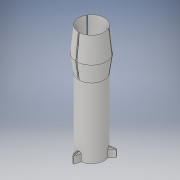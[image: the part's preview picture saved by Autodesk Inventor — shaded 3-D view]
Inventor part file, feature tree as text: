
AUTODESK INVENTOR PART (.ipt)
format: ipt  version: 2017 (Build 210142000, 142)  size: 195,072 bytes
history: native  units: in
note: dims shown in document units (in); Inventor stores cm internally (conversion verified against a paired STEP export)
features: sketch x2, extrude x2, revolve x1, chamfer x1
ambient origin geometry x8: Origin, YZ Plane, XZ Plane, XY Plane, X Axis, Y Axis, Z Axis, Center Point
bodies: Solid1 (feature_tree)
feature tree (6):
  revolve  "Revolution1"  [1 undecoded]
  sketch  "Sketch2"  dims[d2=0.05in d3=1.0in d4=0.1in d5=90.0deg d10=0.025in d11=0.025in d12=0.025in d13=0.025in d14=0.025in d15=0.025in d24=0.24in d25=0.24in d27=0.24in d28=0.24in d29=0.24in d30=0.35in d31=0.0in d32=4.9125in d33=0.0in d34=0.055in d35=0.125in d36=45.0deg]
  extrude  "Extrusion1"  Depth=0.35in
  extrude  "Extrusion2"  Depth=0.35in
  chamfer  "Chamfer1"  Angle=90.0deg  [1 undecoded]
  sketch  "Sketch1"  dims[d0=0.475in d1=3.6in]
note: 2 required parameter values undecoded (feature->parameter linkage not recoverable at this tier; creation-order binding heuristic only, values carry confidence <= 0.55)